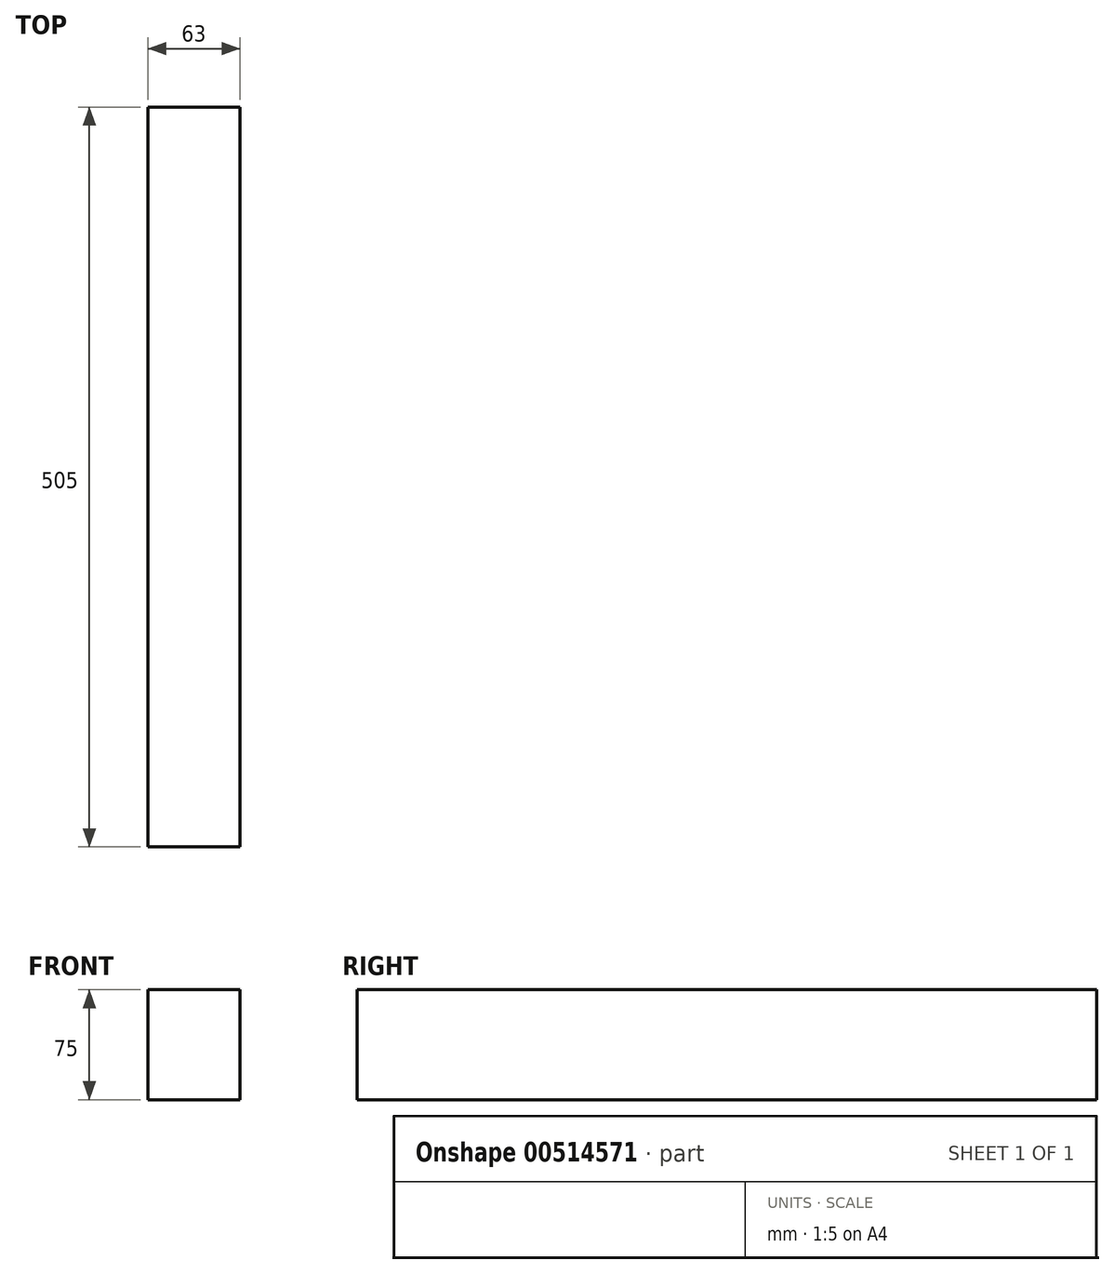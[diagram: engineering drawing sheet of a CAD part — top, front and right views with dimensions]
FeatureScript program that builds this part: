
annotation { "Feature Type Name" : "Feature", "Feature Type Description" : "" }
export const myFeature = defineFeature(function(context is Context, id is Id, definition is map)
    precondition{}
    {
        {
            var Q0;
            Q0=qCreatedBy(makeId("Front.planeOp"),FACE);
            var sketch = newSketch(context, id + "F0", { "sketchPlane" : qUnion([Q0])});
            skLineSegment(sketch, "E0.bottom", {"start": v(31.5, 37.5) * mm, "end": v(-31.5, 37.5) * mm});
            skLineSegment(sketch, "E0.top", {"start": v(31.5, -37.5) * mm, "end": v(-31.5, -37.5) * mm});
            skLineSegment(sketch, "E0.left", {"start": v(31.5, 37.5) * mm, "end": v(31.5, -37.5) * mm});
            skLineSegment(sketch, "E0.right", {"start": v(-31.5, 37.5) * mm, "end": v(-31.5, -37.5) * mm});
            skPoint(sketch, "E0.middle", {"position": v(0, 0) * mm});
            skSolve(sketch);
        }
        {
            var Q0;
            Q0=qSketchRegion(id+"F0",true);
            extrude(context, id + "F1", {"entities" : qUnion([Q0]), "depth" : (700 - 195) * mm, "offsetDistance" : 25 * mm});
        }
    });
